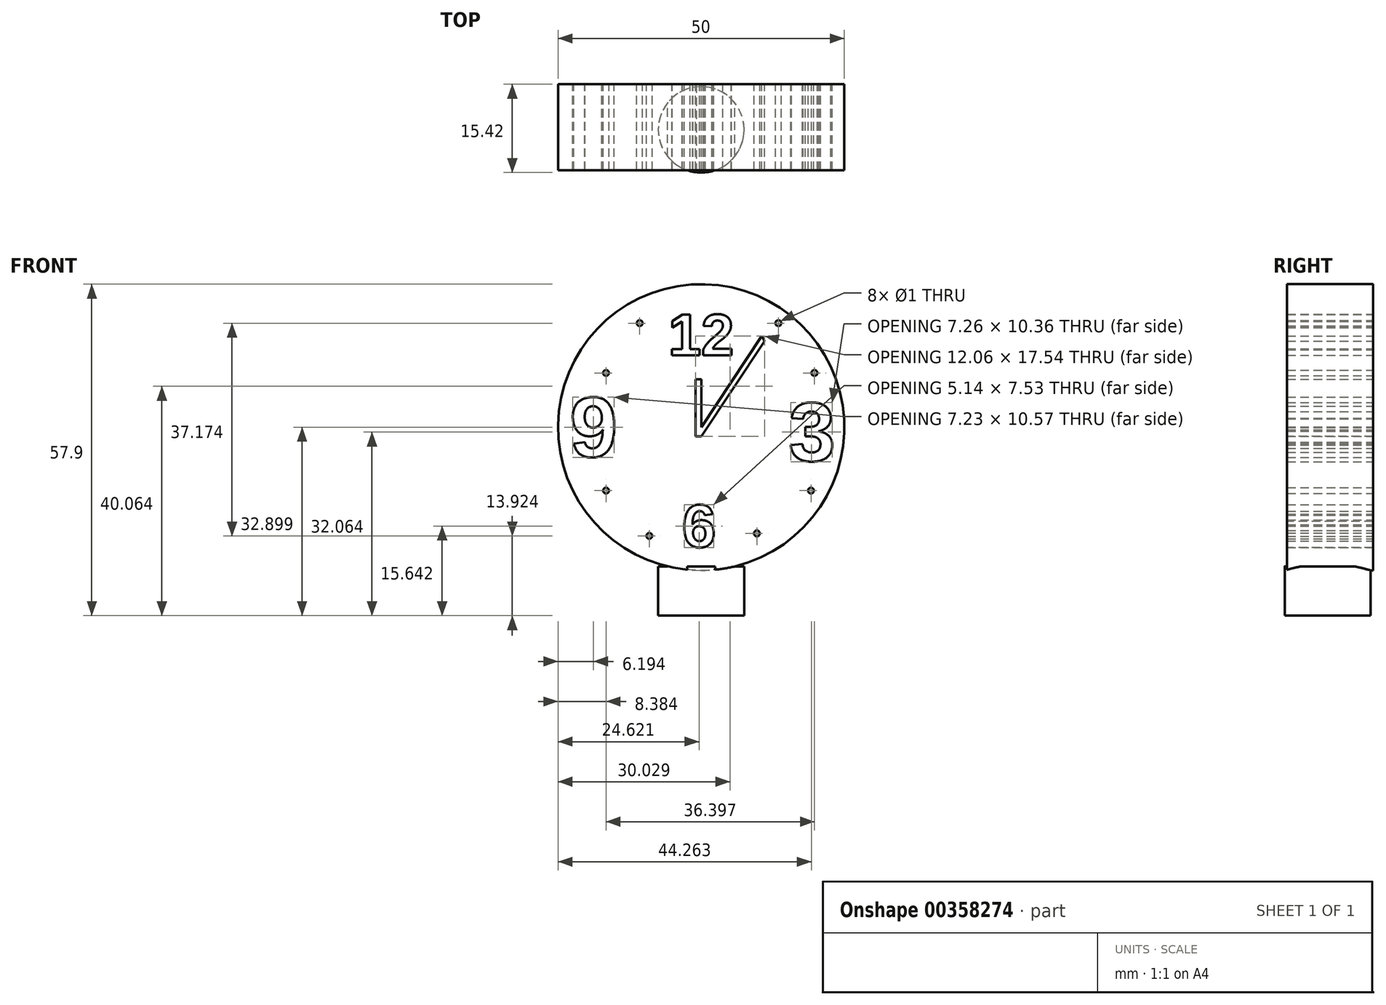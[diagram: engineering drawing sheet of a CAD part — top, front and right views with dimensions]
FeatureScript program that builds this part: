
annotation { "Feature Type Name" : "Feature", "Feature Type Description" : "" }
export const myFeature = defineFeature(function(context is Context, id is Id, definition is map)
    precondition{}
    {
        {
            var Q0;
            Q0=qCreatedBy(makeId("Front.planeOp"),FACE);
            var sketch = newSketch(context, id + "F0", { "sketchPlane" : qUnion([Q0])});
            skCircle(sketch, "E0", {"center": v(0, 0) * mm, "radius": 25 * mm});
            skLineSegment(sketch, "E1", {"start": v(0, 25) * mm, "end": v(0, 20) * mm});
            skLineSegment(sketch, "E2", {"start": v(-30, 0) * mm, "end": v(-25, 0) * mm});
            skLineSegment(sketch, "E3", {"start": v(25, 0) * mm, "end": v(30, 0) * mm});
            skLineSegment(sketch, "E4", {"start": v(0, -20.92) * mm, "end": v(0, -25) * mm});
            skText(sketch, "E5", { "text": "12\n", "fontName": "Arimo-Bold.ttf"});
            skText(sketch, "E6", { "text": "9", "fontName": "Arimo-Bold.ttf"});
            skText(sketch, "E7", { "text": "6", "fontName": "Arimo-Bold.ttf"});
            skText(sketch, "E8", { "text": "3", "fontName": "Arimo-Bold.ttf"});
            skLineSegment(sketch, "E9", {"start": v(0, 0) * mm, "end": v(10.57, 15.93) * mm});
            skLineSegment(sketch, "E10", {"start": v(11.06, 15.06) * mm, "end": v(0, -1.6) * mm});
            skLineSegment(sketch, "E11", {"start": v(0, 0) * mm, "end": v(0, -1.6) * mm});
            skLineSegment(sketch, "E12", {"start": v(10.57, 15.93) * mm, "end": v(11.06, 15.06) * mm});
            skLineSegment(sketch, "E13", {"start": v(0, -1.6) * mm, "end": v(-1, -1.6) * mm});
            skLineSegment(sketch, "E14", {"start": v(-1, -1.6) * mm, "end": v(-1, 8.4) * mm});
            skLineSegment(sketch, "E15", {"start": v(-1, 8.4) * mm, "end": v(0, 8.4) * mm});
            skLineSegment(sketch, "E16", {"start": v(0, 8.4) * mm, "end": v(0, -1.6) * mm});
            skPoint(sketch, "E17", {"position": v(-10.75, 18.2) * mm});
            skPoint(sketch, "E18", {"position": v(-16.62, 9.5) * mm});
            skPoint(sketch, "E19", {"position": v(-16.62, -11.06) * mm});
            skPoint(sketch, "E20", {"position": v(-9.06, -18.98) * mm});
            skPoint(sketch, "E21", {"position": v(9.73, -18.54) * mm});
            skPoint(sketch, "E22", {"position": v(19.18, -11.06) * mm});
            skPoint(sketch, "E23", {"position": v(13.5, 18.2) * mm});
            skPoint(sketch, "E24", {"position": v(19.78, 9.5) * mm});
            skCircle(sketch, "E25", {"center": v(-10.75, 18.2) * mm, "radius": 0.5 * mm});
            skCircle(sketch, "E26", {"center": v(-16.62, 9.5) * mm, "radius": 0.5 * mm});
            skCircle(sketch, "E27", {"center": v(-16.62, -11.06) * mm, "radius": 0.5 * mm});
            skCircle(sketch, "E28", {"center": v(-9.06, -18.98) * mm, "radius": 0.5 * mm});
            skCircle(sketch, "E29", {"center": v(9.73, -18.54) * mm, "radius": 0.5 * mm});
            skCircle(sketch, "E30", {"center": v(19.18, -11.06) * mm, "radius": 0.5 * mm});
            skCircle(sketch, "E31", {"center": v(19.78, 9.5) * mm, "radius": 0.5 * mm});
            skCircle(sketch, "E32", {"center": v(13.5, 18.2) * mm, "radius": 0.5 * mm});
            const initialGuessF0  = {"E5": [-0.00573, 0.01258, 1, 0, 0.00742], "E6": [-0.02294, -0.00514, 1, 0, 0.01075], "E7": [-0.00334, -0.02092, 1, 0, 0.00766], "E8": [0.0153, -0.00585, 1, 0, 0.01051]};
            skSetInitialGuess(sketch, initialGuessF0);
            skSolve(sketch);
        }
        {
            var Q0;
            Q0=makeQuery(id+"F0.imprint","IMPRINT",FACE,{"disambiguationData":[TD([[makeQuery(id+"F0.imprint","IMPRINT",EDGE,{"derivedFrom":sQuery(id+"F0.wireOp",EDGE,"E6.sketch_text.stroke-16")}),1.0]])]});
            var Q1;
            Q1=makeQuery(id+"F0.imprint","IMPRINT",FACE,{"disambiguationData":[TD([[makeQuery(id+"F0.imprint","IMPRINT",EDGE,{"derivedFrom":sQuery(id+"F0.wireOp",EDGE,"E7.sketch_text.stroke-16")}),1.0]])]});
            var Q2;
            Q2=makeQuery(id+"F0.imprint","IMPRINT",FACE,{"disambiguationData":[TD([[makeQuery(id+"F0.imprint","IMPRINT",EDGE,{"derivedFrom":sQuery(id+"F0.wireOp",EDGE,"E5.sketch_text.stroke-0")}),1.0]])]});
            extrude(context, id + "F1", {"entities" : qUnion([Q0, Q1, Q2]), "depth" : 15 * mm});
        }
        {
            var Q0;
            Q0=qCreatedBy(makeId("Top.planeOp"),FACE);
            var sketch = newSketch(context, id + "F2", { "sketchPlane" : qUnion([Q0])});
            skCircle(sketch, "E33", {"center": v(0, -7.92) * mm, "radius": 7.5 * mm});
            skSolve(sketch);
        }
        {
            var Q0;
            Q0 = qSketchRegion(id + "F2", true);
            extrude(context, id + "F3", {"entities" : qUnion([Q0]), "operationType" : NewBodyOperationType.ADD, "oppositeDirection" : true, "depth" : 32.9 * mm, "hasSecondDirection" : true, "secondDirectionOppositeDirection" : true, "secondDirectionDepth" : 24.3 * mm});
        }
    });
